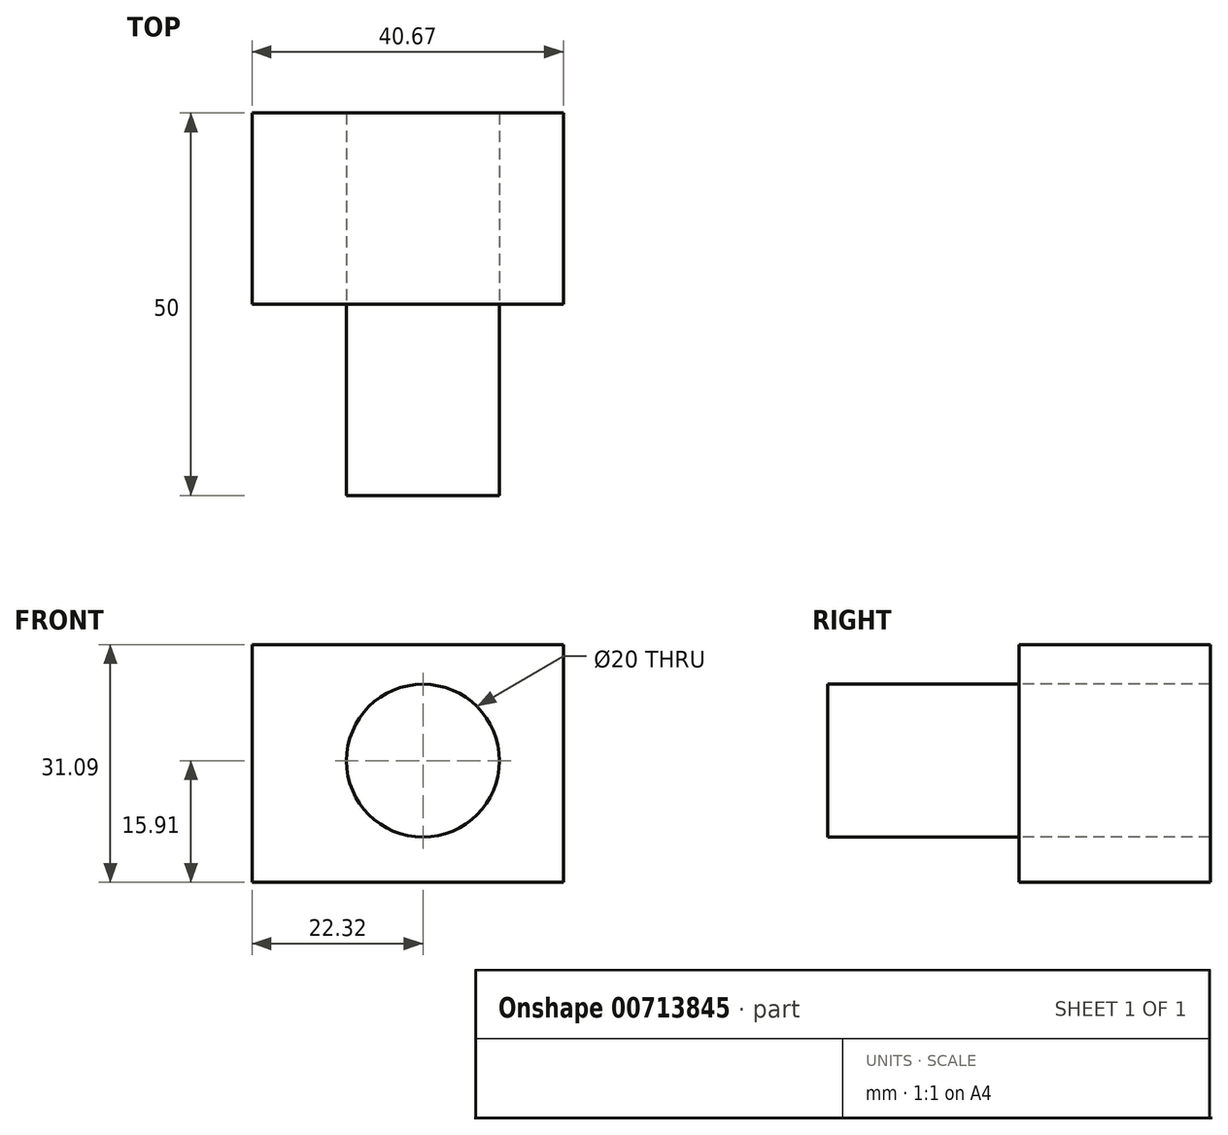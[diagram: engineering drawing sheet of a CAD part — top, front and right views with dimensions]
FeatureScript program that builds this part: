
annotation { "Feature Type Name" : "Feature", "Feature Type Description" : "" }
export const myFeature = defineFeature(function(context is Context, id is Id, definition is map)
    precondition{}
    {
        {
            var Q0;
            Q0=qCreatedBy(makeId("Front.planeOp"),FACE);
            var sketch = newSketch(context, id + "F0", { "sketchPlane" : qUnion([Q0])});
            skCircle(sketch, "E0", {"center": v(0, 0) * mm, "radius": 10 * mm});
            skSolve(sketch);
        }
        {
            var Q0;
            Q0=makeQuery(id+"F0.imprint","IMPRINT",FACE,{"disambiguationData":[TD([[makeQuery(id+"F0.imprint","IMPRINT",EDGE,{"derivedFrom":sQuery(id+"F0.wireOp",EDGE,"E0")}),1.0]])]});
            extrude(context, id + "F1", {"entities" : qUnion([Q0]), "depth" : 25 * mm, "offsetDistance" : 25 * mm});
        }
        {
            var Q0;
            Q0=makeQuery(id+"F1.opExtrude","CAP_FACE",FACE,{"disambiguationData":[OSD([sQuery(id+"F0.wireOp",EDGE,"E0")])],"isStart":true});
            var sketch = newSketch(context, id + "F2", { "sketchPlane" : qUnion([Q0])});
            skLineSegment(sketch, "E1.bottom", {"start": v(22.32, 15.18) * mm, "end": v(-18.35, 15.18) * mm});
            skLineSegment(sketch, "E1.top", {"start": v(22.32, -15.9) * mm, "end": v(-18.35, -15.9) * mm});
            skLineSegment(sketch, "E1.left", {"start": v(22.32, 15.18) * mm, "end": v(22.32, -15.9) * mm});
            skLineSegment(sketch, "E1.right", {"start": v(-18.35, 15.18) * mm, "end": v(-18.35, -15.9) * mm});
            skSolve(sketch);
        }
        {
            var Q0;
            Q0=makeQuery(id+"F2.imprint","IMPRINT",FACE,{"disambiguationData":[TD([[makeQuery(id+"F2.imprint","IMPRINT",EDGE,{"derivedFrom":sQuery(id+"F2.wireOp",EDGE,"E1.bottom")}),1.0]])]});
            extrude(context, id + "F3", {"entities" : qUnion([Q0]), "depth" : 25 * mm, "offsetDistance" : 25 * mm});
        }
    });
